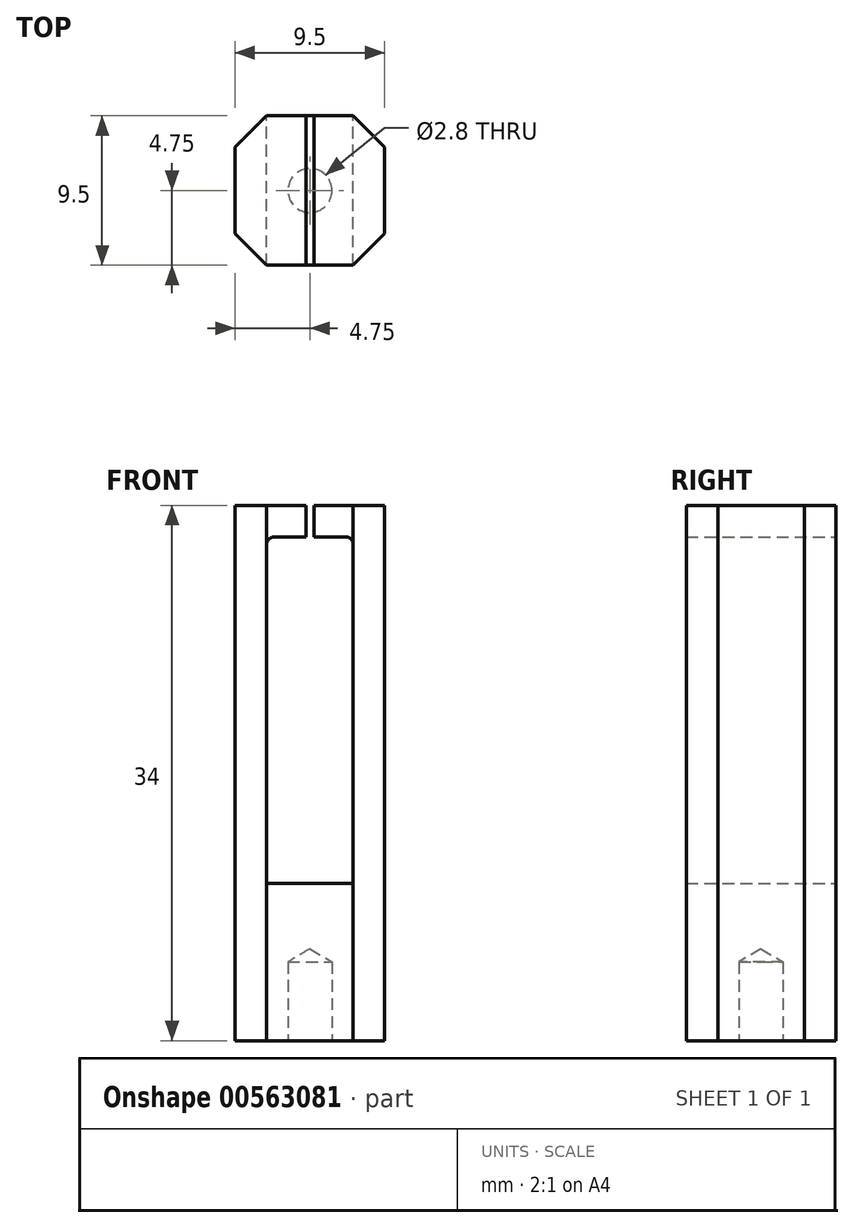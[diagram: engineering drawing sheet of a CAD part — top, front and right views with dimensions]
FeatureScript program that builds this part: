
annotation { "Feature Type Name" : "Feature", "Feature Type Description" : "" }
export const myFeature = defineFeature(function(context is Context, id is Id, definition is map)
    precondition{}
    {
        {
            var Q0;
            Q0=qCreatedBy(makeId("Front.planeOp"),FACE);
            var sketch = newSketch(context, id + "F0", { "sketchPlane" : qUnion([Q0])});
            skLineSegment(sketch, "E0.bottom", {"start": v(0, 0) * mm, "end": v(9.5, 0) * mm});
            skLineSegment(sketch, "E0.top", {"start": v(0, 10) * mm, "end": v(9.5, 10) * mm});
            skLineSegment(sketch, "E0.left", {"start": v(0, 0) * mm, "end": v(0, 10) * mm});
            skLineSegment(sketch, "E0.right", {"start": v(9.5, 0) * mm, "end": v(9.5, 10) * mm});
            skSolve(sketch);
        }
        {
            var Q0;
            Q0=makeQuery(id+"F0.imprint","IMPRINT",FACE,{"disambiguationData":[TD([[makeQuery(id+"F0.imprint","IMPRINT",EDGE,{"derivedFrom":sQuery(id+"F0.wireOp",EDGE,"E0.bottom")}),1.0]])]});
            extrude(context, id + "F1", {"entities" : qUnion([Q0]), "depth" : 9.5 * mm, "offsetDistance" : 25 * mm});
        }
        {
            var Q0;
            Q0=qCreatedBy(makeId("Front.planeOp"),FACE);
            var sketch = newSketch(context, id + "F2", { "sketchPlane" : qUnion([Q0])});
            skLineSegment(sketch, "E1", {"start": v(9.5, 10) * mm, "end": v(9.5, 34) * mm});
            skLineSegment(sketch, "E2", {"start": v(9.5, 34) * mm, "end": v(5, 34) * mm});
            skLineSegment(sketch, "E3", {"start": v(5, 34) * mm, "end": v(5, 32) * mm});
            skLineSegment(sketch, "E4", {"start": v(5, 32) * mm, "end": v(7.5, 32) * mm});
            skLineSegment(sketch, "E5", {"start": v(7.5, 32) * mm, "end": v(7.5, 10) * mm});
            skLineSegment(sketch, "E6", {"start": v(7.5, 10) * mm, "end": v(9.5, 10) * mm});
            skSolve(sketch);
        }
        {
            var Q0;
            Q0=makeQuery(id+"F2.imprint","IMPRINT",FACE,{"disambiguationData":[TD([[makeQuery(id+"F2.imprint","IMPRINT",EDGE,{"derivedFrom":sQuery(id+"F2.wireOp",EDGE,"E1")}),1.0]])]});
            extrude(context, id + "F3", {"entities" : qUnion([Q0]), "depth" : 9.5 * mm, "offsetDistance" : 25 * mm});
        }
        {
            var Q0;
            Q0=makeQuery(id+"F1.opExtrude","SWEPT_FACE",FACE,{"disambiguationData":[OSD([sQuery(id+"F0.wireOp",EDGE,"E0.left")])]});
            cPlane(context, id + "F4", {"entities" : qUnion([Q0]), "cplaneType" : CPlaneType.OFFSET, "offset" : 4.75 * mm, "oppositeDirection" : true, "width" : 150 * mm, "height" : 150 * mm});
        }
        {
            var Q0;
            Q0=makeQuery(id+"F3.opExtrude","SWEPT_BODY",BODY,{"disambiguationData":[OSD([sQuery(id+"F2.wireOp",EDGE,"E1"),sQuery(id+"F2.wireOp",EDGE,"E2"),sQuery(id+"F2.wireOp",EDGE,"E3"),sQuery(id+"F2.wireOp",EDGE,"E4"),sQuery(id+"F2.wireOp",EDGE,"E5"),sQuery(id+"F2.wireOp",EDGE,"E6")])]});
            var Q1;
            Q1=qCreatedBy(id+"F4.planeOp",FACE);
            mirror(context, id + "F5", {"entities" : qUnion([Q0]), "mirrorPlane" : qUnion([Q1])});
        }
        {
            var Q0;
            Q0=makeQuery(id+"F1.opExtrude","SWEPT_BODY",BODY,{"disambiguationData":[OSD([sQuery(id+"F0.wireOp",EDGE,"E0.bottom"),sQuery(id+"F0.wireOp",EDGE,"E0.top"),sQuery(id+"F0.wireOp",EDGE,"E0.left"),sQuery(id+"F0.wireOp",EDGE,"E0.right")])]});
            var Q1;
            Q1=makeQuery(id+"F3.opExtrude","SWEPT_BODY",BODY,{"disambiguationData":[OSD([sQuery(id+"F2.wireOp",EDGE,"E1"),sQuery(id+"F2.wireOp",EDGE,"E2"),sQuery(id+"F2.wireOp",EDGE,"E3"),sQuery(id+"F2.wireOp",EDGE,"E4"),sQuery(id+"F2.wireOp",EDGE,"E5"),sQuery(id+"F2.wireOp",EDGE,"E6")])]});
            booleanBodies(context, id + "F6", {"operationType" : BooleanOperationType.UNION, "tools" : qUnion([Q0, Q1])});
        }
        {
            var Q0;
            Q0=makeQuery(id+"F1.opExtrude","SWEPT_BODY",BODY,{"disambiguationData":[OSD([sQuery(id+"F0.wireOp",EDGE,"E0.bottom"),sQuery(id+"F0.wireOp",EDGE,"E0.top"),sQuery(id+"F0.wireOp",EDGE,"E0.left"),sQuery(id+"F0.wireOp",EDGE,"E0.right")])]});
            var Q1;
            Q1=makeQuery(id+"F5.opPattern","COPY",BODY,{"derivedFrom":makeQuery(id+"F3.opExtrude","SWEPT_BODY",BODY,{"disambiguationData":[OSD([sQuery(id+"F2.wireOp",EDGE,"E1"),sQuery(id+"F2.wireOp",EDGE,"E2"),sQuery(id+"F2.wireOp",EDGE,"E3"),sQuery(id+"F2.wireOp",EDGE,"E4"),sQuery(id+"F2.wireOp",EDGE,"E5"),sQuery(id+"F2.wireOp",EDGE,"E6")])]}),"instanceName":"1"});
            booleanBodies(context, id + "F7", {"operationType" : BooleanOperationType.UNION, "tools" : qUnion([Q0, Q1])});
        }
        {
            var Q0;
            Q0=makeQuery(id+"F6.opBoolean","MERGE",EDGE,{"derivedFrom":[makeQuery(id+"F1.opExtrude","CAP_EDGE",EDGE,{"disambiguationData":[OSD([sQuery(id+"F0.wireOp",EDGE,"E0.right")])],"isStart":false}),makeQuery(id+"F3.opExtrude","CAP_EDGE",EDGE,{"disambiguationData":[OSD([sQuery(id+"F2.wireOp",EDGE,"E1")])],"isStart":false})]});
            var Q1;
            Q1=makeQuery(id+"F6.opBoolean","MERGE",EDGE,{"derivedFrom":[makeQuery(id+"F1.opExtrude","CAP_EDGE",EDGE,{"disambiguationData":[OSD([sQuery(id+"F0.wireOp",EDGE,"E0.right")])],"isStart":true}),makeQuery(id+"F3.opExtrude","CAP_EDGE",EDGE,{"disambiguationData":[OSD([sQuery(id+"F2.wireOp",EDGE,"E1")])],"isStart":true})]});
            var Q2;
            Q2=makeQuery(id+"F7.opBoolean","MERGE",EDGE,{"derivedFrom":[makeQuery(id+"F1.opExtrude","CAP_EDGE",EDGE,{"disambiguationData":[OSD([sQuery(id+"F0.wireOp",EDGE,"E0.left")])],"isStart":false}),makeQuery(id+"F5.opPattern","COPY",EDGE,{"derivedFrom":makeQuery(id+"F3.opExtrude","CAP_EDGE",EDGE,{"disambiguationData":[OSD([sQuery(id+"F2.wireOp",EDGE,"E1")])],"isStart":false}),"instanceName":"1"})]});
            var Q3;
            Q3=makeQuery(id+"F7.opBoolean","MERGE",EDGE,{"derivedFrom":[makeQuery(id+"F1.opExtrude","CAP_EDGE",EDGE,{"disambiguationData":[OSD([sQuery(id+"F0.wireOp",EDGE,"E0.left")])],"isStart":true}),makeQuery(id+"F5.opPattern","COPY",EDGE,{"derivedFrom":makeQuery(id+"F3.opExtrude","CAP_EDGE",EDGE,{"disambiguationData":[OSD([sQuery(id+"F2.wireOp",EDGE,"E1")])],"isStart":true}),"instanceName":"1"})]});
            chamfer(context, id + "F8", {"entities" : qUnion([Q0, Q1, Q2, Q3]), "width" : 2 * mm, "tangentPropagation" : true});
        }
        {
            var Q0;
            Q0=makeQuery(id+"F1.opExtrude","SWEPT_FACE",FACE,{"disambiguationData":[OSD([sQuery(id+"F0.wireOp",EDGE,"E0.bottom")])]});
            var sketch = newSketch(context, id + "F9", { "sketchPlane" : qUnion([Q0])});
            skLineSegment(sketch, "E7", {"start": v(0, 4.75) * mm, "end": v(9.5, 4.75) * mm});
            skPoint(sketch, "E8", {"position": v(4.75, 4.75) * mm});
            skSolve(sketch);
        }
        {
            var Q0;
            Q0=sQuery(id+"F9.wireOp",VERTEX,"E8");
            var Q1;
            Q1=makeQuery(id+"F1.opExtrude","SWEPT_BODY",BODY,{"disambiguationData":[OSD([sQuery(id+"F0.wireOp",EDGE,"E0.bottom"),sQuery(id+"F0.wireOp",EDGE,"E0.top"),sQuery(id+"F0.wireOp",EDGE,"E0.left"),sQuery(id+"F0.wireOp",EDGE,"E0.right")])]});
            hole(context, id + "F10", {"style" : HoleStyle.SIMPLE, "endStyle" : HoleEndStyle.BLIND, "holeDiameter" : 2.8 * mm, "holeDepth" : 5 * mm, "isTappedThrough" : true, "tappedDepth" : 12 * mm, "tapClearance" : 3, "locations" : qUnion([Q0]), "scope" : qUnion([Q1])});
        }
        {
            var Q0;
            Q0=makeQuery(id+"F5.opPattern","COPY",EDGE,{"derivedFrom":makeQuery(id+"F3.opExtrude","SWEPT_EDGE",EDGE,{"disambiguationData":[OSD([sQuery(id+"F2.wireOp",EDGE,"E5"),sQuery(id+"F2.wireOp",EDGE,"E6")])]}),"instanceName":"1"});
            var Q1;
            Q1=makeQuery(id+"F3.opExtrude","SWEPT_EDGE",EDGE,{"disambiguationData":[OSD([sQuery(id+"F2.wireOp",EDGE,"E5"),sQuery(id+"F2.wireOp",EDGE,"E6")])]});
            var Q2;
            Q2=makeQuery(id+"F5.opPattern","COPY",EDGE,{"derivedFrom":makeQuery(id+"F3.opExtrude","SWEPT_EDGE",EDGE,{"disambiguationData":[OSD([sQuery(id+"F2.wireOp",EDGE,"E4"),sQuery(id+"F2.wireOp",EDGE,"E5")])]}),"instanceName":"1"});
            var Q3;
            Q3=makeQuery(id+"F3.opExtrude","SWEPT_EDGE",EDGE,{"disambiguationData":[OSD([sQuery(id+"F2.wireOp",EDGE,"E4"),sQuery(id+"F2.wireOp",EDGE,"E5")])]});
            fillet(context, id + "F11", {"entities" : qUnion([Q0, Q1, Q2, Q3]), "radius" : 0.5 * mm, "tangentPropagation" : true, "allowEdgeOverflow" : false});
        }
    });
